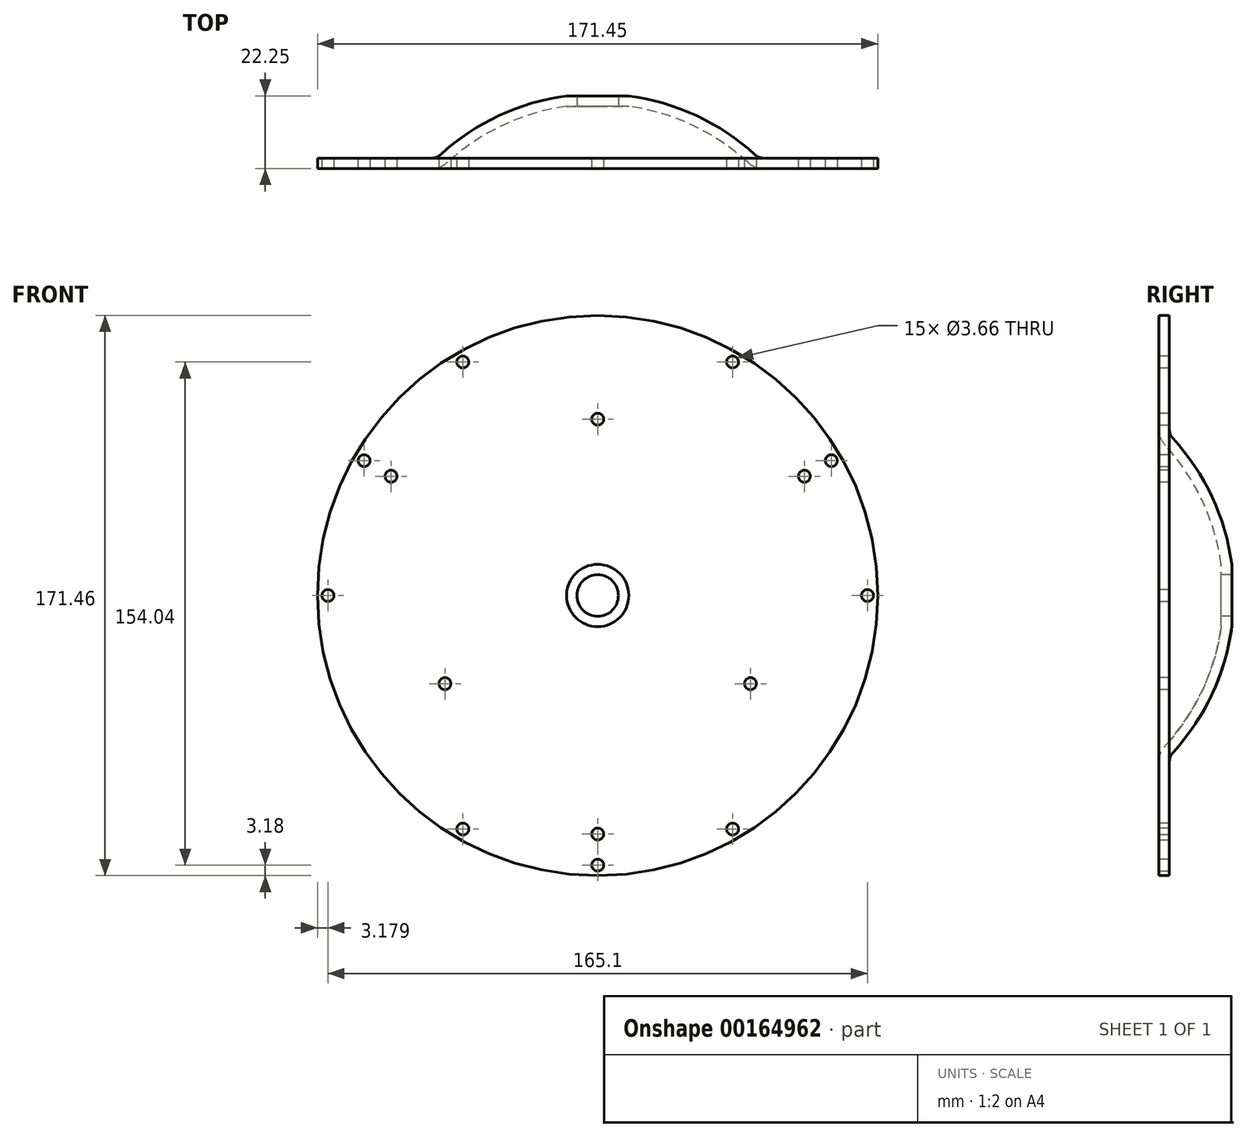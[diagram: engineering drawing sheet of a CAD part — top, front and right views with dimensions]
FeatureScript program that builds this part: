
annotation { "Feature Type Name" : "Feature", "Feature Type Description" : "" }
export const myFeature = defineFeature(function(context is Context, id is Id, definition is map)
    precondition{}
    {
        {
            var Q0;
            Q0=qCreatedBy(makeId("Top.planeOp"),FACE);
            var sketch = newSketch(context, id + "F0", { "sketchPlane" : qUnion([Q0])});
            skArc(sketch, "E0", {"start": v(0, 0) * mm, "mid": v(-16.93, 11.35) * mm, "end": v(-36.46, 17.18) * mm});
            skLineSegment(sketch, "E1", {"start": v(-36.46, 17.18) * mm, "end": v(-36.46, 20.38) * mm, "construction": true});
            skLineSegment(sketch, "E2", {"start": v(4.82, -1.87) * mm, "end": v(39.74, -1.87) * mm});
            skLineSegment(sketch, "E3", {"start": v(39.74, -1.87) * mm, "end": v(39.74, 1.3) * mm});
            skLineSegment(sketch, "E4", {"start": v(39.74, 1.3) * mm, "end": v(4.82, 1.3) * mm});
            skArc(sketch, "E5", {"start": v(2.14, 2.34) * mm, "mid": v(-15.78, 14.31) * mm, "end": v(-36.46, 20.38) * mm});
            skArc(sketch, "E6", {"start": v(2.14, 2.34) * mm, "mid": v(3.38, 1.57) * mm, "end": v(4.82, 1.3) * mm});
            skArc(sketch, "E7", {"start": v(0, 0) * mm, "mid": v(2.23, -1.39) * mm, "end": v(4.82, -1.87) * mm});
            skLineSegment(sketch, "E8", {"start": v(4.82, -1.87) * mm, "end": v(-45.98, -1.87) * mm, "construction": true});
            skLineSegment(sketch, "E9", {"start": v(-45.98, -1.87) * mm, "end": v(-45.98, 17.18) * mm, "construction": true});
            skLineSegment(sketch, "E10", {"start": v(4.82, -1.87) * mm, "end": v(4.82, 1.3) * mm, "construction": true});
            skLineSegment(sketch, "E11.bottom", {"start": v(-45.98, 17.18) * mm, "end": v(-36.46, 17.18) * mm});
            skLineSegment(sketch, "E11.top", {"start": v(-45.98, 20.38) * mm, "end": v(-36.46, 20.38) * mm});
            skLineSegment(sketch, "E11.left", {"start": v(-45.98, 17.18) * mm, "end": v(-45.98, 20.38) * mm});
            skSolve(sketch);
        }
        {
            var Q0;
            Q0 = qSketchRegion(id + "F0", true);
            var Q1;
            Q1=sQuery(id+"F0.wireOp",EDGE,"E9");
            revolve(context, id + "F1", {"entities" : qUnion([Q0]), "axis" : qUnion([Q1]), "revolveType" : RevolveType.FULL});
        }
        {
            var Q0;
            Q0=makeQuery(id+"F1.opRevolve","SWEPT_FACE",FACE,{"disambiguationData":[OSD([sQuery(id+"F0.wireOp",EDGE,"E2")])]});
            var sketch = newSketch(context, id + "F2", { "sketchPlane" : qUnion([Q0])});
            skCircle(sketch, "E12.cCircle", {"center": v(-45.98, 0) * mm, "radius": 71.5 * mm, "construction": true});
            skLineSegment(sketch, "E12.0", {"start": v(-87.26, 71.5) * mm, "end": v(-4.7, 71.5) * mm, "construction": true});
            skLineSegment(sketch, "E12.1", {"start": v(-4.7, 71.5) * mm, "end": v(36.57, 0) * mm, "construction": true});
            skLineSegment(sketch, "E12.2", {"start": v(36.57, 0) * mm, "end": v(-4.7, -71.5) * mm, "construction": true});
            skLineSegment(sketch, "E12.3", {"start": v(-4.7, -71.5) * mm, "end": v(-87.26, -71.5) * mm, "construction": true});
            skLineSegment(sketch, "E12.4", {"start": v(-87.26, -71.5) * mm, "end": v(-128.53, 0) * mm, "construction": true});
            skLineSegment(sketch, "E12.5", {"start": v(-128.53, 0) * mm, "end": v(-87.26, 71.5) * mm, "construction": true});
            skPoint(sketch, "E12.0.midPoint", {"position": v(-45.98, 71.5) * mm});
            skCircle(sketch, "E13.cCircle", {"center": v(-45.98, 0) * mm, "radius": 41.27 * mm, "construction": true});
            skLineSegment(sketch, "E13.0", {"start": v(-117.47, 41.27) * mm, "end": v(25.5, 41.27) * mm, "construction": true});
            skLineSegment(sketch, "E13.1", {"start": v(25.5, 41.28) * mm, "end": v(-45.98, -82.55) * mm, "construction": true});
            skLineSegment(sketch, "E13.2", {"start": v(-45.98, -82.55) * mm, "end": v(-117.47, 41.28) * mm, "construction": true});
            skPoint(sketch, "E13.0.midPoint", {"position": v(-45.98, 41.27) * mm});
            skCircle(sketch, "E14", {"center": v(-4.7, 71.5) * mm, "radius": 3.18 * mm, "construction": true});
            skCircle(sketch, "E15", {"center": v(25.5, 41.28) * mm, "radius": 3.18 * mm, "construction": true});
            skCircle(sketch, "E16", {"center": v(-87.26, 71.5) * mm, "radius": 1.83 * mm});
            skCircle(sketch, "E17", {"center": v(-4.7, 71.5) * mm, "radius": 1.83 * mm});
            skCircle(sketch, "E18", {"center": v(36.57, 0) * mm, "radius": 1.83 * mm});
            skCircle(sketch, "E19", {"center": v(-4.7, -71.5) * mm, "radius": 1.83 * mm});
            skCircle(sketch, "E20", {"center": v(-87.26, -71.5) * mm, "radius": 1.83 * mm});
            skCircle(sketch, "E21", {"center": v(-128.53, 0) * mm, "radius": 1.83 * mm});
            skCircle(sketch, "E22", {"center": v(-117.47, 41.28) * mm, "radius": 1.83 * mm});
            skCircle(sketch, "E23", {"center": v(25.5, 41.28) * mm, "radius": 1.83 * mm});
            skCircle(sketch, "E24", {"center": v(-45.98, -82.55) * mm, "radius": 1.83 * mm});
            skSolve(sketch);
        }
        {
            var Q0;
            Q0 = qSketchRegion(id + "F2", true);
            var Q1;
            Q1=makeQuery(id+"F1.opRevolve","SWEPT_FACE",FACE,{"disambiguationData":[OSD([sQuery(id+"F0.wireOp",EDGE,"E4")])]});
            extrude(context, id + "F3", {"entities" : qUnion([Q0]), "operationType" : NewBodyOperationType.REMOVE, "endBound" : BoundingType.UP_TO_SURFACE, "oppositeDirection" : true, "endBoundEntityFace" : qUnion([Q1]), "depth" : 25.4 * mm});
        }
        {
            var Q0;
            Q0=makeQuery(id+"F1.opRevolve","SWEPT_FACE",FACE,{"disambiguationData":[OSD([sQuery(id+"F0.wireOp",EDGE,"E2")])]});
            var sketch = newSketch(context, id + "F4", { "sketchPlane" : qUnion([Q0])});
            skCircle(sketch, "E25.cCircle", {"center": v(-45.98, 0) * mm, "radius": 36.51 * mm, "construction": true});
            skLineSegment(sketch, "E25.0", {"start": v(-109.22, 36.51) * mm, "end": v(17.26, 36.51) * mm, "construction": true});
            skLineSegment(sketch, "E25.1", {"start": v(17.26, 36.51) * mm, "end": v(-45.98, -73.03) * mm, "construction": true});
            skLineSegment(sketch, "E25.2", {"start": v(-45.98, -73.02) * mm, "end": v(-109.22, 36.51) * mm, "construction": true});
            skLineSegment(sketch, "E26", {"start": v(-45.98, -82.55) * mm, "end": v(-45.98, -73.03) * mm, "construction": true});
            skCircle(sketch, "E27", {"center": v(-109.22, 36.51) * mm, "radius": 1.83 * mm});
            skCircle(sketch, "E28", {"center": v(17.26, 36.51) * mm, "radius": 1.83 * mm});
            skCircle(sketch, "E29", {"center": v(-45.98, -73.03) * mm, "radius": 1.83 * mm});
            skCircle(sketch, "E30", {"center": v(-45.98, 0) * mm, "radius": 6.35 * mm});
            skCircle(sketch, "E31.cCircle", {"center": v(-45.98, 0) * mm, "radius": 26.99 * mm, "construction": true});
            skLineSegment(sketch, "E31.0", {"start": v(0.76, -26.99) * mm, "end": v(-92.72, -26.99) * mm, "construction": true});
            skLineSegment(sketch, "E31.1", {"start": v(-92.72, -26.99) * mm, "end": v(-45.98, 53.98) * mm, "construction": true});
            skLineSegment(sketch, "E31.2", {"start": v(-45.98, 53.98) * mm, "end": v(0.76, -26.99) * mm, "construction": true});
            skCircle(sketch, "E32", {"center": v(-45.98, 53.98) * mm, "radius": 3.18 * mm, "construction": true});
            skCircle(sketch, "E33", {"center": v(-45.98, 53.98) * mm, "radius": 1.83 * mm});
            skCircle(sketch, "E34", {"center": v(-92.72, -26.99) * mm, "radius": 1.83 * mm});
            skCircle(sketch, "E35", {"center": v(0.76, -26.99) * mm, "radius": 1.83 * mm});
            skSolve(sketch);
        }
        {
            var Q0;
            Q0 = qSketchRegion(id + "F4", true);
            var Q1;
            Q1=makeQuery(id+"F1.opRevolve","SWEPT_FACE",FACE,{"disambiguationData":[OSD([sQuery(id+"F0.wireOp",EDGE,"E11.top")])]});
            extrude(context, id + "F5", {"entities" : qUnion([Q0]), "operationType" : NewBodyOperationType.REMOVE, "endBound" : BoundingType.UP_TO_SURFACE, "oppositeDirection" : true, "endBoundEntityFace" : qUnion([Q1]), "depth" : 25.4 * mm});
        }
    });
